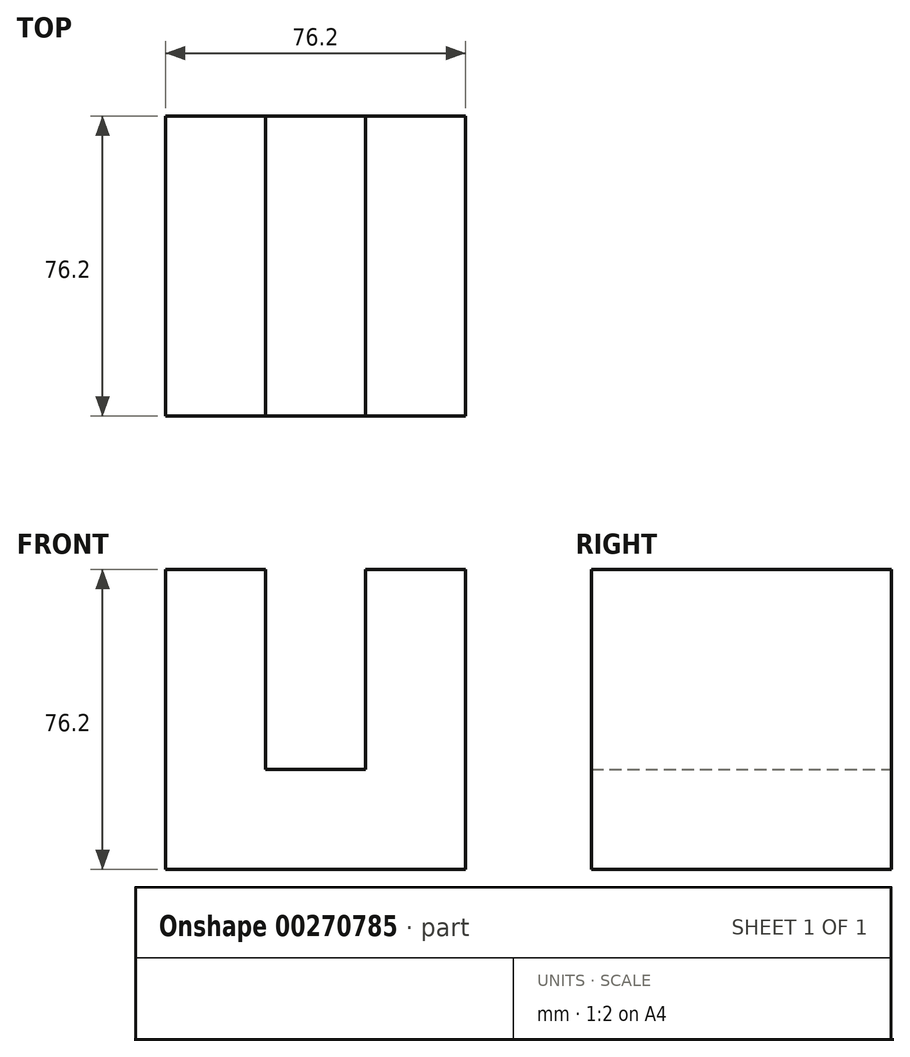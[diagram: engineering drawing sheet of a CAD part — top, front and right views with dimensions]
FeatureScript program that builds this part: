
annotation { "Feature Type Name" : "Feature", "Feature Type Description" : "" }
export const myFeature = defineFeature(function(context is Context, id is Id, definition is map)
    precondition{}
    {
        {
            var Q0;
            Q0=qCreatedBy(makeId("Front.planeOp"),FACE);
            var sketch = newSketch(context, id + "F0", { "sketchPlane" : qUnion([Q0])});
            skLineSegment(sketch, "E0", {"start": v(-59.77, 50.8) * mm, "end": v(-59.77, -25.4) * mm});
            skLineSegment(sketch, "E1", {"start": v(-59.77, -25.4) * mm, "end": v(16.43, -25.4) * mm});
            skLineSegment(sketch, "E2", {"start": v(16.43, -25.4) * mm, "end": v(16.43, 50.8) * mm});
            skLineSegment(sketch, "E3", {"start": v(16.43, 50.8) * mm, "end": v(-8.97, 50.8) * mm});
            skLineSegment(sketch, "E4", {"start": v(-8.97, 50.8) * mm, "end": v(-8.97, 0) * mm});
            skLineSegment(sketch, "E5", {"start": v(-8.97, 0) * mm, "end": v(-34.37, 0) * mm});
            skLineSegment(sketch, "E6", {"start": v(-34.37, 0) * mm, "end": v(-34.37, 50.8) * mm});
            skLineSegment(sketch, "E7", {"start": v(-34.37, 50.8) * mm, "end": v(-59.77, 50.8) * mm});
            skSolve(sketch);
        }
        {
            var Q0;
            Q0 = qSketchRegion(id + "F0", true);
            extrude(context, id + "F1", {"entities" : qUnion([Q0]), "depth" : 76.2 * mm});
        }
    });
